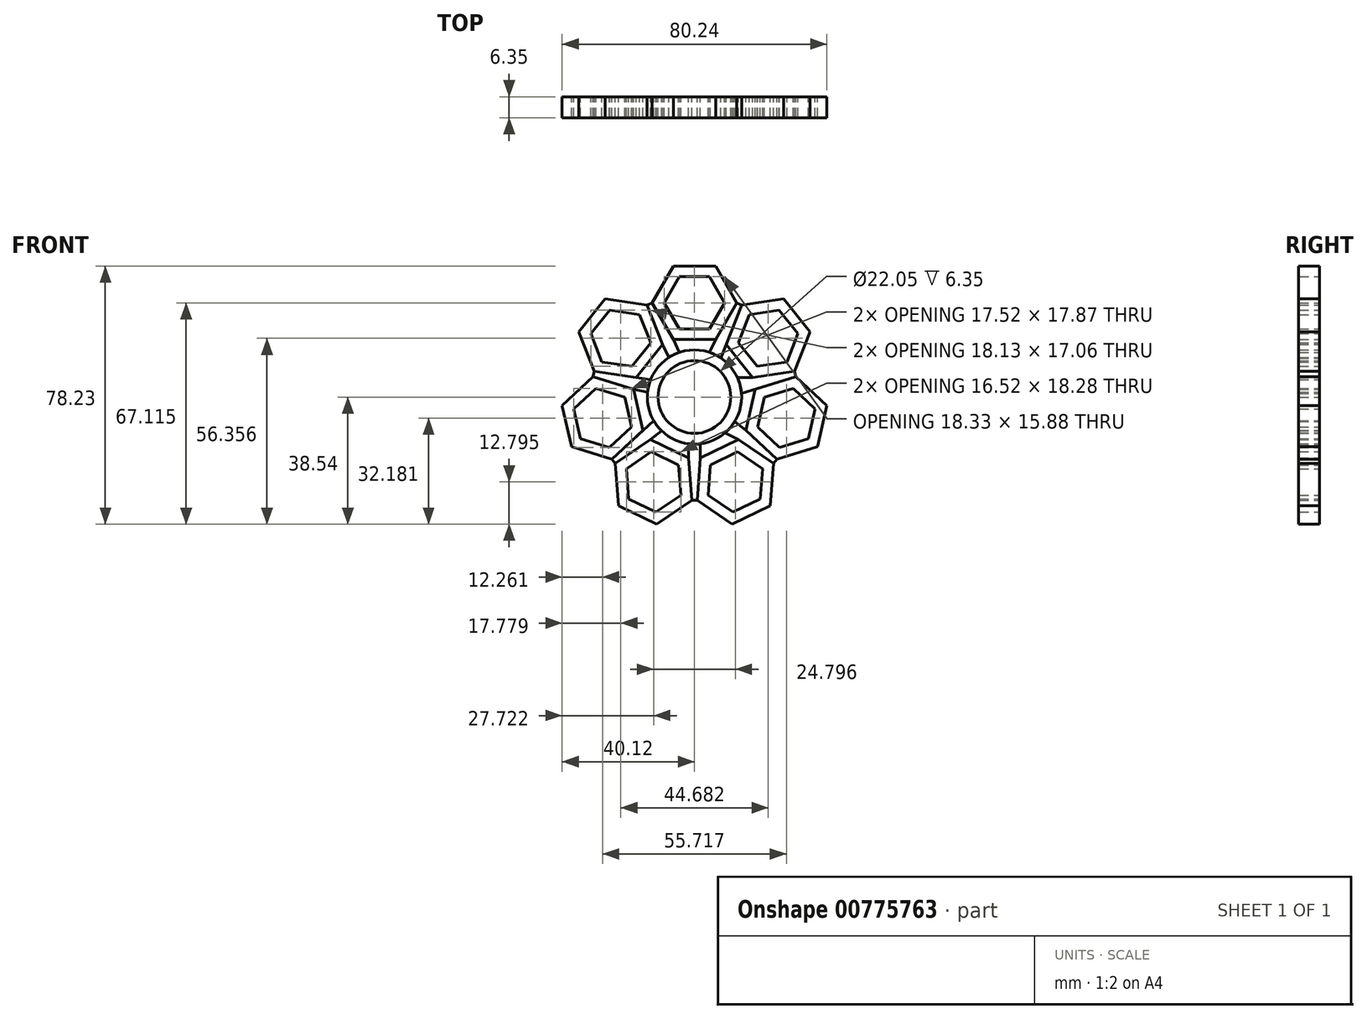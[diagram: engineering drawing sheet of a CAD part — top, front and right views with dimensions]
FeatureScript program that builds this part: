
annotation { "Feature Type Name" : "Feature", "Feature Type Description" : "" }
export const myFeature = defineFeature(function(context is Context, id is Id, definition is map)
    precondition{}
    {
        {
            var Q0;
            Q0=qCreatedBy(makeId("Front.planeOp"),FACE);
            var sketch = newSketch(context, id + "F0", { "sketchPlane" : qUnion([Q0])});
            skCircle(sketch, "E0", {"center": v(0, 0) * mm, "radius": 11.02 * mm});
            skCircle(sketch, "E1", {"center": v(0, 0) * mm, "radius": 14.29 * mm});
            skCircle(sketch, "E2.cCircle", {"center": v(0, 28.58) * mm, "radius": 7.94 * mm, "construction": true});
            skLineSegment(sketch, "E2.0", {"start": v(4.58, 20.64) * mm, "end": v(-4.58, 20.64) * mm});
            skLineSegment(sketch, "E2.1", {"start": v(-4.58, 20.64) * mm, "end": v(-9.17, 28.57) * mm});
            skLineSegment(sketch, "E2.2", {"start": v(-9.17, 28.58) * mm, "end": v(-4.58, 36.51) * mm});
            skLineSegment(sketch, "E2.3", {"start": v(-4.58, 36.51) * mm, "end": v(4.58, 36.51) * mm});
            skLineSegment(sketch, "E2.4", {"start": v(4.58, 36.51) * mm, "end": v(9.17, 28.58) * mm});
            skLineSegment(sketch, "E2.5", {"start": v(9.17, 28.58) * mm, "end": v(4.58, 20.64) * mm});
            skPoint(sketch, "E2.0.midPoint", {"position": v(0, 20.64) * mm});
            skCircle(sketch, "E3.cCircle", {"center": v(0, 28.58) * mm, "radius": 11.11 * mm, "construction": true});
            skLineSegment(sketch, "E3.0", {"start": v(6.42, 17.46) * mm, "end": v(-6.42, 17.46) * mm});
            skLineSegment(sketch, "E3.1", {"start": v(-6.42, 17.46) * mm, "end": v(-12.83, 28.58) * mm});
            skLineSegment(sketch, "E3.2", {"start": v(-12.83, 28.58) * mm, "end": v(-6.42, 39.69) * mm});
            skLineSegment(sketch, "E3.3", {"start": v(-6.42, 39.69) * mm, "end": v(6.42, 39.69) * mm});
            skLineSegment(sketch, "E3.4", {"start": v(6.42, 39.69) * mm, "end": v(12.83, 28.58) * mm});
            skLineSegment(sketch, "E3.5", {"start": v(12.83, 28.57) * mm, "end": v(6.42, 17.46) * mm});
            skPoint(sketch, "E3.0.midPoint", {"position": v(0, 17.46) * mm});
            skLineSegment(sketch, "E4.1.0", {"start": v(-13.28, 16.45) * mm, "end": v(-19, 9.28) * mm});
            skPoint(sketch, "E4.1.1", {"position": v(-13.65, 10.89) * mm});
            skLineSegment(sketch, "E4.1.2", {"start": v(-28.06, 10.65) * mm, "end": v(-31.4, 19.18) * mm});
            skLineSegment(sketch, "E4.1.3", {"start": v(-14.34, 27.85) * mm, "end": v(-9.65, 15.9) * mm});
            skLineSegment(sketch, "E4.1.4", {"start": v(-27.03, 29.76) * mm, "end": v(-14.34, 27.85) * mm});
            skLineSegment(sketch, "E4.1.5", {"start": v(-35.03, 19.73) * mm, "end": v(-27.03, 29.76) * mm});
            skLineSegment(sketch, "E4.1.6", {"start": v(-19, 9.28) * mm, "end": v(-28.06, 10.65) * mm});
            skLineSegment(sketch, "E4.1.7", {"start": v(-31.4, 19.18) * mm, "end": v(-25.69, 26.35) * mm});
            skLineSegment(sketch, "E4.1.8", {"start": v(-25.69, 26.35) * mm, "end": v(-16.63, 24.98) * mm});
            skLineSegment(sketch, "E4.1.9", {"start": v(-16.63, 24.98) * mm, "end": v(-13.28, 16.45) * mm});
            skCircle(sketch, "E4.1.10", {"center": v(-22.34, 17.82) * mm, "radius": 11.11 * mm, "construction": true});
            skLineSegment(sketch, "E4.1.11", {"start": v(-9.65, 15.9) * mm, "end": v(-17.65, 5.87) * mm});
            skLineSegment(sketch, "E4.1.12", {"start": v(-17.65, 5.87) * mm, "end": v(-30.34, 7.78) * mm});
            skLineSegment(sketch, "E4.1.13", {"start": v(-30.34, 7.78) * mm, "end": v(-35.03, 19.73) * mm});
            skPoint(sketch, "E4.1.14", {"position": v(-16.14, 12.87) * mm});
            skCircle(sketch, "E4.1.15", {"center": v(-22.34, 17.82) * mm, "radius": 7.94 * mm, "construction": true});
            skLineSegment(sketch, "E4.2.0", {"start": v(-21.14, -0.12) * mm, "end": v(-19.1, -9.06) * mm});
            skPoint(sketch, "E4.2.1", {"position": v(-17.02, -3.89) * mm});
            skLineSegment(sketch, "E4.2.2", {"start": v(-25.82, -15.3) * mm, "end": v(-34.58, -12.6) * mm});
            skLineSegment(sketch, "E4.2.3", {"start": v(-30.71, 6.15) * mm, "end": v(-18.45, 2.37) * mm});
            skLineSegment(sketch, "E4.2.4", {"start": v(-40.12, -2.58) * mm, "end": v(-30.71, 6.15) * mm});
            skLineSegment(sketch, "E4.2.5", {"start": v(-37.26, -15.09) * mm, "end": v(-40.12, -2.58) * mm});
            skLineSegment(sketch, "E4.2.6", {"start": v(-19.1, -9.06) * mm, "end": v(-25.82, -15.3) * mm});
            skLineSegment(sketch, "E4.2.7", {"start": v(-34.58, -12.6) * mm, "end": v(-36.62, -3.66) * mm});
            skLineSegment(sketch, "E4.2.8", {"start": v(-36.62, -3.66) * mm, "end": v(-29.9, 2.58) * mm});
            skLineSegment(sketch, "E4.2.9", {"start": v(-29.9, 2.58) * mm, "end": v(-21.14, -0.12) * mm});
            skCircle(sketch, "E4.2.10", {"center": v(-27.86, -6.36) * mm, "radius": 11.11 * mm, "construction": true});
            skLineSegment(sketch, "E4.2.11", {"start": v(-18.45, 2.37) * mm, "end": v(-15.6, -10.14) * mm});
            skLineSegment(sketch, "E4.2.12", {"start": v(-15.6, -10.14) * mm, "end": v(-25, -18.87) * mm});
            skLineSegment(sketch, "E4.2.13", {"start": v(-25, -18.87) * mm, "end": v(-37.26, -15.09) * mm});
            skPoint(sketch, "E4.2.14", {"position": v(-20.12, -4.6) * mm});
            skCircle(sketch, "E4.2.15", {"center": v(-27.86, -6.36) * mm, "radius": 7.94 * mm, "construction": true});
            skLineSegment(sketch, "E4.3.0", {"start": v(-13.08, -16.6) * mm, "end": v(-4.83, -20.58) * mm});
            skPoint(sketch, "E4.3.1", {"position": v(-7.58, -15.73) * mm});
            skLineSegment(sketch, "E4.3.2", {"start": v(-4.14, -29.72) * mm, "end": v(-11.71, -34.88) * mm});
            skLineSegment(sketch, "E4.3.3", {"start": v(-23.96, -20.18) * mm, "end": v(-13.36, -12.95) * mm});
            skLineSegment(sketch, "E4.3.4", {"start": v(-23, -32.97) * mm, "end": v(-23.96, -20.18) * mm});
            skLineSegment(sketch, "E4.3.5", {"start": v(-11.44, -38.54) * mm, "end": v(-23, -32.97) * mm});
            skLineSegment(sketch, "E4.3.6", {"start": v(-4.83, -20.58) * mm, "end": v(-4.14, -29.72) * mm});
            skLineSegment(sketch, "E4.3.7", {"start": v(-11.71, -34.88) * mm, "end": v(-19.97, -30.9) * mm});
            skLineSegment(sketch, "E4.3.8", {"start": v(-19.97, -30.9) * mm, "end": v(-20.66, -21.77) * mm});
            skLineSegment(sketch, "E4.3.9", {"start": v(-20.66, -21.77) * mm, "end": v(-13.08, -16.6) * mm});
            skCircle(sketch, "E4.3.10", {"center": v(-12.4, -25.75) * mm, "radius": 11.11 * mm, "construction": true});
            skLineSegment(sketch, "E4.3.11", {"start": v(-13.36, -12.95) * mm, "end": v(-1.8, -18.52) * mm});
            skLineSegment(sketch, "E4.3.12", {"start": v(-1.8, -18.52) * mm, "end": v(-0.84, -31.31) * mm});
            skLineSegment(sketch, "E4.3.13", {"start": v(-0.84, -31.31) * mm, "end": v(-11.44, -38.54) * mm});
            skPoint(sketch, "E4.3.14", {"position": v(-8.95, -18.6) * mm});
            skCircle(sketch, "E4.3.15", {"center": v(-12.4, -25.75) * mm, "radius": 7.94 * mm, "construction": true});
            skLineSegment(sketch, "E4.4.0", {"start": v(4.83, -20.58) * mm, "end": v(13.08, -16.6) * mm});
            skPoint(sketch, "E4.4.1", {"position": v(7.58, -15.73) * mm});
            skLineSegment(sketch, "E4.4.2", {"start": v(20.66, -21.77) * mm, "end": v(19.97, -30.9) * mm});
            skLineSegment(sketch, "E4.4.3", {"start": v(0.84, -31.31) * mm, "end": v(1.8, -18.52) * mm});
            skLineSegment(sketch, "E4.4.4", {"start": v(11.44, -38.54) * mm, "end": v(0.84, -31.31) * mm});
            skLineSegment(sketch, "E4.4.5", {"start": v(23, -32.97) * mm, "end": v(11.44, -38.54) * mm});
            skLineSegment(sketch, "E4.4.6", {"start": v(13.08, -16.6) * mm, "end": v(20.66, -21.77) * mm});
            skLineSegment(sketch, "E4.4.7", {"start": v(19.97, -30.9) * mm, "end": v(11.71, -34.88) * mm});
            skLineSegment(sketch, "E4.4.8", {"start": v(11.71, -34.88) * mm, "end": v(4.14, -29.72) * mm});
            skLineSegment(sketch, "E4.4.9", {"start": v(4.14, -29.72) * mm, "end": v(4.83, -20.58) * mm});
            skCircle(sketch, "E4.4.10", {"center": v(12.4, -25.75) * mm, "radius": 11.11 * mm, "construction": true});
            skLineSegment(sketch, "E4.4.11", {"start": v(1.8, -18.52) * mm, "end": v(13.36, -12.95) * mm});
            skLineSegment(sketch, "E4.4.12", {"start": v(13.36, -12.95) * mm, "end": v(23.96, -20.18) * mm});
            skLineSegment(sketch, "E4.4.13", {"start": v(23.96, -20.18) * mm, "end": v(23, -32.97) * mm});
            skPoint(sketch, "E4.4.14", {"position": v(8.95, -18.6) * mm});
            skCircle(sketch, "E4.4.15", {"center": v(12.4, -25.75) * mm, "radius": 7.94 * mm, "construction": true});
            skLineSegment(sketch, "E4.5.0", {"start": v(19.1, -9.06) * mm, "end": v(21.14, -0.12) * mm});
            skPoint(sketch, "E4.5.1", {"position": v(17.02, -3.89) * mm});
            skLineSegment(sketch, "E4.5.2", {"start": v(29.9, 2.58) * mm, "end": v(36.62, -3.66) * mm});
            skLineSegment(sketch, "E4.5.3", {"start": v(25, -18.87) * mm, "end": v(15.6, -10.14) * mm});
            skLineSegment(sketch, "E4.5.4", {"start": v(37.26, -15.09) * mm, "end": v(25, -18.87) * mm});
            skLineSegment(sketch, "E4.5.5", {"start": v(40.12, -2.58) * mm, "end": v(37.26, -15.09) * mm});
            skLineSegment(sketch, "E4.5.6", {"start": v(21.14, -0.12) * mm, "end": v(29.9, 2.58) * mm});
            skLineSegment(sketch, "E4.5.7", {"start": v(36.62, -3.66) * mm, "end": v(34.58, -12.6) * mm});
            skLineSegment(sketch, "E4.5.8", {"start": v(34.58, -12.6) * mm, "end": v(25.82, -15.3) * mm});
            skLineSegment(sketch, "E4.5.9", {"start": v(25.82, -15.3) * mm, "end": v(19.1, -9.06) * mm});
            skCircle(sketch, "E4.5.10", {"center": v(27.86, -6.36) * mm, "radius": 11.11 * mm, "construction": true});
            skLineSegment(sketch, "E4.5.11", {"start": v(15.6, -10.14) * mm, "end": v(18.45, 2.37) * mm});
            skLineSegment(sketch, "E4.5.12", {"start": v(18.45, 2.37) * mm, "end": v(30.71, 6.15) * mm});
            skLineSegment(sketch, "E4.5.13", {"start": v(30.71, 6.15) * mm, "end": v(40.12, -2.58) * mm});
            skPoint(sketch, "E4.5.14", {"position": v(20.12, -4.6) * mm});
            skCircle(sketch, "E4.5.15", {"center": v(27.86, -6.36) * mm, "radius": 7.94 * mm, "construction": true});
            skLineSegment(sketch, "E4.6.0", {"start": v(19, 9.28) * mm, "end": v(13.28, 16.45) * mm});
            skPoint(sketch, "E4.6.1", {"position": v(13.65, 10.89) * mm});
            skLineSegment(sketch, "E4.6.2", {"start": v(16.63, 24.98) * mm, "end": v(25.69, 26.35) * mm});
            skLineSegment(sketch, "E4.6.3", {"start": v(30.34, 7.78) * mm, "end": v(17.65, 5.87) * mm});
            skLineSegment(sketch, "E4.6.4", {"start": v(35.03, 19.73) * mm, "end": v(30.34, 7.78) * mm});
            skLineSegment(sketch, "E4.6.5", {"start": v(27.03, 29.76) * mm, "end": v(35.03, 19.73) * mm});
            skLineSegment(sketch, "E4.6.6", {"start": v(13.28, 16.45) * mm, "end": v(16.63, 24.98) * mm});
            skLineSegment(sketch, "E4.6.7", {"start": v(25.69, 26.35) * mm, "end": v(31.4, 19.18) * mm});
            skLineSegment(sketch, "E4.6.8", {"start": v(31.4, 19.18) * mm, "end": v(28.06, 10.65) * mm});
            skLineSegment(sketch, "E4.6.9", {"start": v(28.06, 10.65) * mm, "end": v(19, 9.28) * mm});
            skCircle(sketch, "E4.6.10", {"center": v(22.34, 17.82) * mm, "radius": 11.11 * mm, "construction": true});
            skLineSegment(sketch, "E4.6.11", {"start": v(17.65, 5.87) * mm, "end": v(9.65, 15.9) * mm});
            skLineSegment(sketch, "E4.6.12", {"start": v(9.65, 15.9) * mm, "end": v(14.34, 27.85) * mm});
            skLineSegment(sketch, "E4.6.13", {"start": v(14.34, 27.85) * mm, "end": v(27.03, 29.76) * mm});
            skPoint(sketch, "E4.6.14", {"position": v(16.14, 12.87) * mm});
            skCircle(sketch, "E4.6.15", {"center": v(22.34, 17.82) * mm, "radius": 7.94 * mm, "construction": true});
            skSolve(sketch);
        }
        {
            var Q0;
            Q0=qCreatedBy(makeId("Front.planeOp"),FACE);
            var sketch = newSketch(context, id + "F1", { "sketchPlane" : qUnion([Q0])});
            skLineSegment(sketch, "E5.0", {"start": v(-19.1, -9.06) * mm, "end": v(-25.82, -15.3) * mm});
            skCircle(sketch, "E5.1", {"center": v(22.34, 17.82) * mm, "radius": 7.94 * mm});
            skLineSegment(sketch, "E5.2", {"start": v(-19.97, -30.9) * mm, "end": v(-20.66, -21.77) * mm});
            skLineSegment(sketch, "E5.3", {"start": v(18.45, 2.37) * mm, "end": v(30.71, 6.15) * mm});
            skCircle(sketch, "E5.4", {"center": v(12.4, -25.75) * mm, "radius": 11.11 * mm});
            skLineSegment(sketch, "E5.5", {"start": v(-27.03, 29.76) * mm, "end": v(-14.34, 27.85) * mm});
            skLineSegment(sketch, "E5.6", {"start": v(25, -18.87) * mm, "end": v(15.6, -10.14) * mm});
            skLineSegment(sketch, "E5.7", {"start": v(27.03, 29.76) * mm, "end": v(35.03, 19.73) * mm});
            skLineSegment(sketch, "E5.8", {"start": v(-9.65, 15.9) * mm, "end": v(-17.65, 5.87) * mm});
            skLineSegment(sketch, "E5.9", {"start": v(-25, -18.87) * mm, "end": v(-37.26, -15.09) * mm});
            skLineSegment(sketch, "E5.10", {"start": v(4.83, -20.58) * mm, "end": v(13.08, -16.6) * mm});
            skLineSegment(sketch, "E5.11", {"start": v(20.66, -21.77) * mm, "end": v(19.97, -30.9) * mm});
            skCircle(sketch, "E5.12", {"center": v(-27.86, -6.36) * mm, "radius": 7.94 * mm});
            skLineSegment(sketch, "E5.13", {"start": v(-17.65, 5.87) * mm, "end": v(-30.34, 7.78) * mm});
            skLineSegment(sketch, "E5.14", {"start": v(13.28, 16.45) * mm, "end": v(16.63, 24.98) * mm});
            skLineSegment(sketch, "E5.15", {"start": v(37.26, -15.09) * mm, "end": v(25, -18.87) * mm});
            skLineSegment(sketch, "E5.16", {"start": v(-35.03, 19.73) * mm, "end": v(-27.03, 29.76) * mm});
            skLineSegment(sketch, "E5.17", {"start": v(30.71, 6.15) * mm, "end": v(40.12, -2.58) * mm});
            skLineSegment(sketch, "E5.18", {"start": v(21.14, -0.12) * mm, "end": v(29.9, 2.58) * mm});
            skLineSegment(sketch, "E5.19", {"start": v(11.44, -38.54) * mm, "end": v(0.84, -31.31) * mm});
            skLineSegment(sketch, "E5.20", {"start": v(1.8, -18.52) * mm, "end": v(13.36, -12.95) * mm});
            skLineSegment(sketch, "E5.21", {"start": v(-4.14, -29.72) * mm, "end": v(-11.71, -34.88) * mm});
            skLineSegment(sketch, "E5.22", {"start": v(-20.66, -21.77) * mm, "end": v(-13.08, -16.6) * mm});
            skLineSegment(sketch, "E5.23", {"start": v(-34.58, -12.6) * mm, "end": v(-36.62, -3.66) * mm});
            skCircle(sketch, "E5.24", {"center": v(-22.34, 17.82) * mm, "radius": 7.94 * mm});
            skLineSegment(sketch, "E5.25", {"start": v(31.4, 19.18) * mm, "end": v(28.06, 10.65) * mm});
            skLineSegment(sketch, "E5.26", {"start": v(0.84, -31.31) * mm, "end": v(1.8, -18.52) * mm});
            skLineSegment(sketch, "E5.27", {"start": v(-13.08, -16.6) * mm, "end": v(-4.83, -20.58) * mm});
            skLineSegment(sketch, "E5.28", {"start": v(-30.34, 7.78) * mm, "end": v(-35.03, 19.73) * mm});
            skLineSegment(sketch, "E5.29", {"start": v(25.69, 26.35) * mm, "end": v(31.4, 19.18) * mm});
            skLineSegment(sketch, "E5.30", {"start": v(40.12, -2.58) * mm, "end": v(37.26, -15.09) * mm});
            skLineSegment(sketch, "E5.31", {"start": v(-19, 9.28) * mm, "end": v(-28.06, 10.65) * mm});
            skLineSegment(sketch, "E5.32", {"start": v(36.62, -3.66) * mm, "end": v(34.58, -12.6) * mm});
            skCircle(sketch, "E5.33", {"center": v(27.86, -6.36) * mm, "radius": 7.94 * mm});
            skLineSegment(sketch, "E5.34", {"start": v(23, -32.97) * mm, "end": v(11.44, -38.54) * mm});
            skLineSegment(sketch, "E5.35", {"start": v(13.36, -12.95) * mm, "end": v(23.96, -20.18) * mm});
            skCircle(sketch, "E5.36", {"center": v(-12.4, -25.75) * mm, "radius": 11.11 * mm});
            skLineSegment(sketch, "E5.37", {"start": v(-23.96, -20.18) * mm, "end": v(-13.36, -12.95) * mm});
            skLineSegment(sketch, "E5.38", {"start": v(-21.14, -0.12) * mm, "end": v(-19.1, -9.06) * mm});
            skLineSegment(sketch, "E5.39", {"start": v(-36.62, -3.66) * mm, "end": v(-29.9, 2.58) * mm});
            skLineSegment(sketch, "E5.40", {"start": v(28.06, 10.65) * mm, "end": v(19, 9.28) * mm});
            skLineSegment(sketch, "E5.41", {"start": v(-31.4, 19.18) * mm, "end": v(-25.69, 26.35) * mm});
            skLineSegment(sketch, "E5.42", {"start": v(34.58, -12.6) * mm, "end": v(25.82, -15.3) * mm});
            skLineSegment(sketch, "E5.43", {"start": v(19, 9.28) * mm, "end": v(13.28, 16.45) * mm});
            skLineSegment(sketch, "E5.44", {"start": v(13.08, -16.6) * mm, "end": v(20.66, -21.77) * mm});
            skLineSegment(sketch, "E5.45", {"start": v(23.96, -20.18) * mm, "end": v(23, -32.97) * mm});
            skLineSegment(sketch, "E5.46", {"start": v(-23, -32.97) * mm, "end": v(-23.96, -20.18) * mm});
            skLineSegment(sketch, "E5.47", {"start": v(-13.36, -12.95) * mm, "end": v(-1.8, -18.52) * mm});
            skLineSegment(sketch, "E5.48", {"start": v(-25.82, -15.3) * mm, "end": v(-34.58, -12.6) * mm});
            skLineSegment(sketch, "E5.49", {"start": v(-29.9, 2.58) * mm, "end": v(-21.14, -0.12) * mm});
            skCircle(sketch, "E5.50", {"center": v(22.34, 17.82) * mm, "radius": 11.11 * mm});
            skLineSegment(sketch, "E5.51", {"start": v(-6.42, 39.69) * mm, "end": v(6.42, 39.69) * mm});
            skLineSegment(sketch, "E5.52", {"start": v(6.42, 39.69) * mm, "end": v(12.83, 28.58) * mm});
            skLineSegment(sketch, "E5.53", {"start": v(12.83, 28.57) * mm, "end": v(6.42, 17.46) * mm});
            skCircle(sketch, "E5.54", {"center": v(0, 0) * mm, "radius": 11.02 * mm});
            skCircle(sketch, "E5.55", {"center": v(0, 0) * mm, "radius": 14.29 * mm});
            skCircle(sketch, "E5.56", {"center": v(0, 28.58) * mm, "radius": 7.94 * mm});
            skLineSegment(sketch, "E5.57", {"start": v(4.58, 20.64) * mm, "end": v(-4.58, 20.64) * mm});
            skLineSegment(sketch, "E5.58", {"start": v(-4.58, 20.64) * mm, "end": v(-9.17, 28.57) * mm});
            skLineSegment(sketch, "E5.59", {"start": v(-9.17, 28.58) * mm, "end": v(-4.58, 36.51) * mm});
            skLineSegment(sketch, "E5.60", {"start": v(-4.58, 36.51) * mm, "end": v(4.58, 36.51) * mm});
            skLineSegment(sketch, "E5.61", {"start": v(4.58, 36.51) * mm, "end": v(9.17, 28.58) * mm});
            skLineSegment(sketch, "E5.62", {"start": v(9.17, 28.58) * mm, "end": v(4.58, 20.64) * mm});
            skCircle(sketch, "E5.63", {"center": v(0, 28.58) * mm, "radius": 11.11 * mm});
            skLineSegment(sketch, "E5.64", {"start": v(6.42, 17.46) * mm, "end": v(-6.42, 17.46) * mm});
            skLineSegment(sketch, "E5.65", {"start": v(-6.42, 17.46) * mm, "end": v(-12.83, 28.58) * mm});
            skLineSegment(sketch, "E5.66", {"start": v(-12.83, 28.58) * mm, "end": v(-6.42, 39.69) * mm});
            skLineSegment(sketch, "E5.67", {"start": v(17.65, 5.87) * mm, "end": v(9.65, 15.9) * mm});
            skLineSegment(sketch, "E5.68", {"start": v(-1.8, -18.52) * mm, "end": v(-0.84, -31.31) * mm});
            skCircle(sketch, "E5.69", {"center": v(-27.86, -6.36) * mm, "radius": 11.11 * mm});
            skLineSegment(sketch, "E5.70", {"start": v(-25.69, 26.35) * mm, "end": v(-16.63, 24.98) * mm});
            skLineSegment(sketch, "E5.71", {"start": v(16.63, 24.98) * mm, "end": v(25.69, 26.35) * mm});
            skCircle(sketch, "E5.72", {"center": v(12.4, -25.75) * mm, "radius": 7.94 * mm});
            skLineSegment(sketch, "E5.73", {"start": v(-13.28, 16.45) * mm, "end": v(-19, 9.28) * mm});
            skLineSegment(sketch, "E5.74", {"start": v(25.82, -15.3) * mm, "end": v(19.1, -9.06) * mm});
            skLineSegment(sketch, "E5.75", {"start": v(19.97, -30.9) * mm, "end": v(11.71, -34.88) * mm});
            skLineSegment(sketch, "E5.76", {"start": v(-11.44, -38.54) * mm, "end": v(-23, -32.97) * mm});
            skLineSegment(sketch, "E5.77", {"start": v(-30.71, 6.15) * mm, "end": v(-18.45, 2.37) * mm});
            skLineSegment(sketch, "E5.78", {"start": v(-0.84, -31.31) * mm, "end": v(-11.44, -38.54) * mm});
            skLineSegment(sketch, "E5.79", {"start": v(-18.45, 2.37) * mm, "end": v(-15.6, -10.14) * mm});
            skLineSegment(sketch, "E5.80", {"start": v(-16.63, 24.98) * mm, "end": v(-13.28, 16.45) * mm});
            skLineSegment(sketch, "E5.81", {"start": v(30.34, 7.78) * mm, "end": v(17.65, 5.87) * mm});
            skLineSegment(sketch, "E5.82", {"start": v(19.1, -9.06) * mm, "end": v(21.14, -0.12) * mm});
            skLineSegment(sketch, "E5.83", {"start": v(-28.06, 10.65) * mm, "end": v(-31.4, 19.18) * mm});
            skCircle(sketch, "E5.84", {"center": v(27.86, -6.36) * mm, "radius": 11.11 * mm});
            skLineSegment(sketch, "E5.85", {"start": v(11.71, -34.88) * mm, "end": v(4.14, -29.72) * mm});
            skLineSegment(sketch, "E5.86", {"start": v(-4.83, -20.58) * mm, "end": v(-4.14, -29.72) * mm});
            skLineSegment(sketch, "E5.87", {"start": v(-40.12, -2.58) * mm, "end": v(-30.71, 6.15) * mm});
            skLineSegment(sketch, "E5.88", {"start": v(9.65, 15.9) * mm, "end": v(14.34, 27.85) * mm});
            skCircle(sketch, "E5.89", {"center": v(-12.4, -25.75) * mm, "radius": 7.94 * mm});
            skLineSegment(sketch, "E5.90", {"start": v(-15.6, -10.14) * mm, "end": v(-25, -18.87) * mm});
            skCircle(sketch, "E5.91", {"center": v(-22.34, 17.82) * mm, "radius": 11.11 * mm});
            skLineSegment(sketch, "E5.92", {"start": v(35.03, 19.73) * mm, "end": v(30.34, 7.78) * mm});
            skLineSegment(sketch, "E5.93", {"start": v(29.9, 2.58) * mm, "end": v(36.62, -3.66) * mm});
            skLineSegment(sketch, "E5.94", {"start": v(-14.34, 27.85) * mm, "end": v(-9.65, 15.9) * mm});
            skLineSegment(sketch, "E5.95", {"start": v(15.6, -10.14) * mm, "end": v(18.45, 2.37) * mm});
            skLineSegment(sketch, "E5.96", {"start": v(4.14, -29.72) * mm, "end": v(4.83, -20.58) * mm});
            skLineSegment(sketch, "E5.97", {"start": v(-11.71, -34.88) * mm, "end": v(-19.97, -30.9) * mm});
            skLineSegment(sketch, "E5.98", {"start": v(-37.26, -15.09) * mm, "end": v(-40.12, -2.58) * mm});
            skLineSegment(sketch, "E5.99", {"start": v(14.34, 27.85) * mm, "end": v(27.03, 29.76) * mm});
            skLineSegment(sketch, "E6", {"start": v(-30.71, 6.15) * mm, "end": v(-30.34, 7.78) * mm});
            skLineSegment(sketch, "E7", {"start": v(-12.83, 28.58) * mm, "end": v(-14.34, 27.85) * mm});
            skLineSegment(sketch, "E8", {"start": v(12.83, 28.58) * mm, "end": v(14.34, 27.85) * mm});
            skLineSegment(sketch, "E9", {"start": v(-25, -18.87) * mm, "end": v(-23.96, -20.18) * mm});
            skLineSegment(sketch, "E10", {"start": v(-0.84, -31.31) * mm, "end": v(0.84, -31.31) * mm});
            skLineSegment(sketch, "E11", {"start": v(23.96, -20.18) * mm, "end": v(25, -18.87) * mm});
            skLineSegment(sketch, "E12", {"start": v(30.71, 6.15) * mm, "end": v(30.34, 7.78) * mm});
            skLineSegment(sketch, "E13", {"start": v(-18.45, 2.37) * mm, "end": v(-17.65, 5.87) * mm});
            skLineSegment(sketch, "E14", {"start": v(-9.65, 15.9) * mm, "end": v(-6.42, 17.46) * mm});
            skLineSegment(sketch, "E15", {"start": v(6.42, 17.46) * mm, "end": v(9.65, 15.9) * mm});
            skLineSegment(sketch, "E16", {"start": v(17.65, 5.87) * mm, "end": v(18.45, 2.37) * mm});
            skLineSegment(sketch, "E17", {"start": v(15.6, -10.14) * mm, "end": v(13.36, -12.95) * mm});
            skLineSegment(sketch, "E18", {"start": v(-1.8, -18.52) * mm, "end": v(1.8, -18.52) * mm});
            skLineSegment(sketch, "E19", {"start": v(-15.6, -10.14) * mm, "end": v(-13.36, -12.95) * mm});
            skLineSegment(sketch, "E20", {"start": v(-9.65, 15.9) * mm, "end": v(-7.77, 12) * mm});
            skLineSegment(sketch, "E21", {"start": v(-6.42, 17.46) * mm, "end": v(-4.53, 13.55) * mm});
            skLineSegment(sketch, "E22", {"start": v(6.42, 17.46) * mm, "end": v(4.53, 13.55) * mm});
            skLineSegment(sketch, "E23", {"start": v(9.65, 15.9) * mm, "end": v(8.04, 11.8) * mm});
            skLineSegment(sketch, "E24", {"start": v(-18.45, 2.37) * mm, "end": v(-14.22, 1.4) * mm});
            skLineSegment(sketch, "E25", {"start": v(-17.65, 5.87) * mm, "end": v(-13.3, 5.22) * mm});
            skLineSegment(sketch, "E26", {"start": v(-15.6, -10.14) * mm, "end": v(-12.37, -7.15) * mm});
            skLineSegment(sketch, "E27", {"start": v(-13.36, -12.95) * mm, "end": v(-9.84, -10.14) * mm});
            skLineSegment(sketch, "E28", {"start": v(-1.8, -18.52) * mm, "end": v(-1.8, -14.17) * mm});
            skLineSegment(sketch, "E29", {"start": v(1.8, -18.52) * mm, "end": v(1.8, -14.17) * mm});
            skLineSegment(sketch, "E30", {"start": v(13.36, -12.95) * mm, "end": v(9.28, -10.86) * mm});
            skLineSegment(sketch, "E31", {"start": v(17.65, 5.87) * mm, "end": v(13.03, 5.87) * mm});
            skLineSegment(sketch, "E32", {"start": v(18.45, 2.37) * mm, "end": v(14.25, 1.07) * mm});
            skLineSegment(sketch, "E33", {"start": v(15.6, -10.14) * mm, "end": v(12.2, -7.43) * mm});
            skSolve(sketch);
        }
        {
            var Q0;
            Q0 = qSketchRegion(id + "F0", true);
            var Q1;
            {var subQ3=sQuery(id+"F1.wireOp",EDGE,"E6");Q1=makeQuery(id+"F1.imprint","IMPRINT",FACE,{"disambiguationData":[TD([[makeQuery(id+"F1.imprint","IMPRINT",EDGE,{"derivedFrom":subQ3}),-1.0]])]});}
            var Q2;
            Q2=makeQuery(id+"F1.imprint","IMPRINT",FACE,{"disambiguationData":[TD([[makeQuery(id+"F1.imprint","IMPRINT",EDGE,{"derivedFrom":sQuery(id+"F1.wireOp",EDGE,"E13")}),-1.0]])]});
            var Q3;
            {var subQ3=sQuery(id+"F1.wireOp",EDGE,"E7");Q3=makeQuery(id+"F1.imprint","IMPRINT",FACE,{"disambiguationData":[TD([[makeQuery(id+"F1.imprint","IMPRINT",EDGE,{"derivedFrom":subQ3}),1.0]])]});}
            var Q4;
            Q4=makeQuery(id+"F1.imprint","IMPRINT",FACE,{"disambiguationData":[TD([[makeQuery(id+"F1.imprint","IMPRINT",EDGE,{"derivedFrom":sQuery(id+"F1.wireOp",EDGE,"E14")}),-1.0]])]});
            var Q5;
            {var subQ0=sQuery(id+"F1.wireOp",EDGE,"E8");Q5=makeQuery(id+"F1.imprint","IMPRINT",FACE,{"disambiguationData":[TD([[makeQuery(id+"F1.imprint","IMPRINT",EDGE,{"derivedFrom":subQ0}),-1.0]])]});}
            var Q6;
            Q6=makeQuery(id+"F1.imprint","IMPRINT",FACE,{"disambiguationData":[TD([[makeQuery(id+"F1.imprint","IMPRINT",EDGE,{"derivedFrom":sQuery(id+"F1.wireOp",EDGE,"E15")}),-1.0]])]});
            var Q7;
            {var subQ3=sQuery(id+"F1.wireOp",EDGE,"E12");Q7=makeQuery(id+"F1.imprint","IMPRINT",FACE,{"disambiguationData":[TD([[makeQuery(id+"F1.imprint","IMPRINT",EDGE,{"derivedFrom":subQ3}),1.0]])]});}
            var Q8;
            Q8=makeQuery(id+"F1.imprint","IMPRINT",FACE,{"disambiguationData":[TD([[makeQuery(id+"F1.imprint","IMPRINT",EDGE,{"derivedFrom":sQuery(id+"F1.wireOp",EDGE,"E16")}),-1.0]])]});
            var Q9;
            {var subQ0=sQuery(id+"F1.wireOp",EDGE,"E11");Q9=makeQuery(id+"F1.imprint","IMPRINT",FACE,{"disambiguationData":[TD([[makeQuery(id+"F1.imprint","IMPRINT",EDGE,{"derivedFrom":subQ0}),1.0]])]});}
            var Q10;
            Q10=makeQuery(id+"F1.imprint","IMPRINT",FACE,{"disambiguationData":[TD([[makeQuery(id+"F1.imprint","IMPRINT",EDGE,{"derivedFrom":sQuery(id+"F1.wireOp",EDGE,"E17")}),-1.0]])]});
            var Q11;
            {var subQ0=sQuery(id+"F1.wireOp",EDGE,"E10");Q11=makeQuery(id+"F1.imprint","IMPRINT",FACE,{"disambiguationData":[TD([[makeQuery(id+"F1.imprint","IMPRINT",EDGE,{"derivedFrom":subQ0}),1.0]])]});}
            var Q12;
            Q12=makeQuery(id+"F1.imprint","IMPRINT",FACE,{"disambiguationData":[TD([[makeQuery(id+"F1.imprint","IMPRINT",EDGE,{"derivedFrom":sQuery(id+"F1.wireOp",EDGE,"E18")}),1.0]])]});
            var Q13;
            {var subQ0=sQuery(id+"F1.wireOp",EDGE,"E9");Q13=makeQuery(id+"F1.imprint","IMPRINT",FACE,{"disambiguationData":[TD([[makeQuery(id+"F1.imprint","IMPRINT",EDGE,{"derivedFrom":subQ0}),1.0]])]});}
            var Q14;
            {var subQ4=sQuery(id+"F1.wireOp",EDGE,"E19");Q14=makeQuery(id+"F1.imprint","IMPRINT",FACE,{"disambiguationData":[TD([[makeQuery(id+"F1.imprint","IMPRINT",EDGE,{"derivedFrom":subQ4}),1.0]])]});}
            extrude(context, id + "F2", {"entities" : qUnion([Q0, Q1, Q2, Q3, Q4, Q5, Q6, Q7, Q8, Q9, Q10, Q11, Q12, Q13, Q14]), "depth" : 6.35 * mm, "offsetDistance" : 25.4 * mm});
        }
    });
